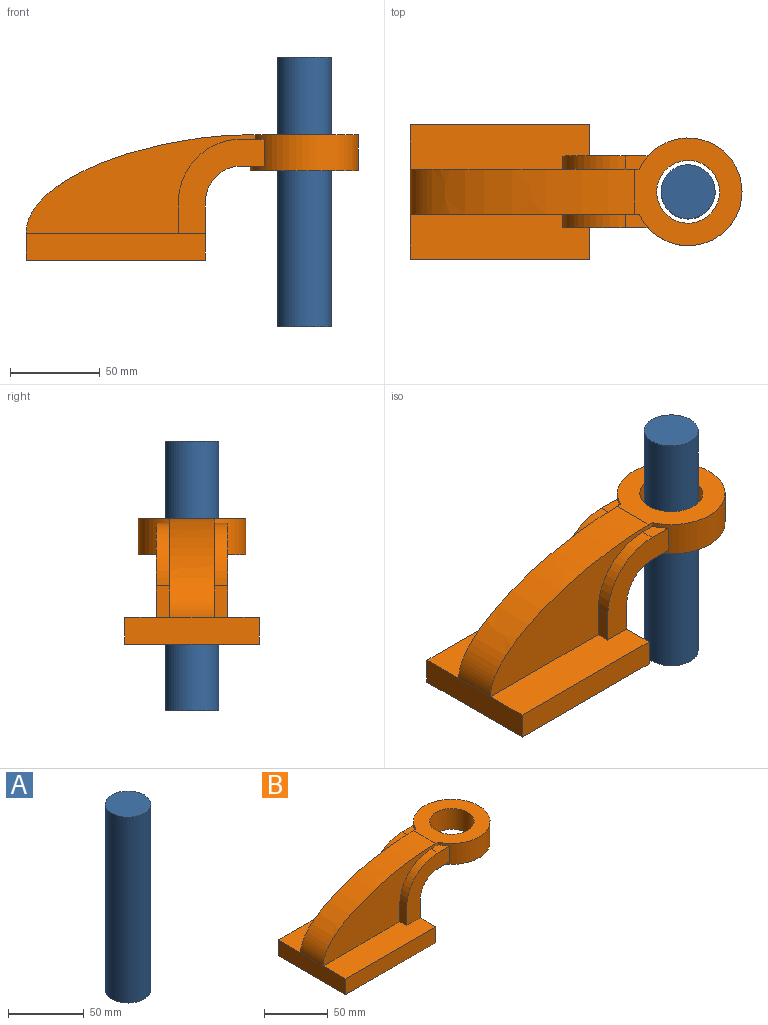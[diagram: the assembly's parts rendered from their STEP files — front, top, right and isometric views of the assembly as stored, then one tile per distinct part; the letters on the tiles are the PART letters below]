
ASSEMBLY  parts=2 mates=1
PART A: 3 faces, bbox 30x30x150 mm
  f0: cylinder r=15mm len=150mm, axis (0,0,-1), area 14137.2mm2, adj f1,f2
  f1: plane 30x30mm, normal (0,0,1), area 706.9mm2, adj f0
  f2: plane 30x30mm, normal (0,0,-1), area 706.9mm2, adj f0
PART B: 24 faces, bbox 185x75x70 mm
  f0: plane 100x25mm, normal (0,0,1), area 2387.5mm2, adj f3,f5,f7,f9,f16,f20
  f1: plane 12.64x7.5mm, normal (0,0,1), area 74.4mm2, adj f2,f16,f20,f22
  f2: cylinder r=35mm len=35mm, axis (0,1,0), area 412.3mm2, adj f1,f3,f16,f20
  f3: plane 17.5x7.5mm, normal (-1,0,0), area 131.2mm2, adj f0,f2,f16,f20
  f4: plane 100x25mm, normal (0,0,1), area 2387.5mm2, adj f5,f7,f8,f14,f15,f19
  f5: plane 75x15mm, normal (-1,0,0), area 1125mm2, adj f0,f4,f6,f8,f9,f17
  f6: plane 100x75mm, normal (0,0,-1), area 7500mm2, adj f5,f7,f8,f9
  f7: plane 75x32.5mm, normal (1,0,0), area 1825mm2, adj f0,f4,f6,f8,f9,f10,f15,f16
  f8: plane 100x15mm, normal (0,-1,0), area 1500mm2, adj f4,f5,f6,f7
  f9: plane 100x15mm, normal (0,1,0), area 1500mm2, adj f0,f5,f6,f7
  f10: cylinder r=20mm len=40mm, axis (0,1,0), area 1256.6mm2, adj f7,f11,f15,f16
  f11: plane 40x12.64mm, normal (0,0,-1), area 296mm2, adj f10,f15,f16,f22
  f12: plane 12.64x7.5mm, normal (0,0,1), area 74.4mm2, adj f13,f15,f19,f22
  f13: cylinder r=35mm len=35mm, axis (0,1,0), area 412.3mm2, adj f12,f14,f15,f19
  f14: plane 17.5x7.5mm, normal (-1,0,0), area 131.2mm2, adj f4,f13,f15,f19
  f15: plane 52.5x47.64mm, normal (0,-1,0), area 1100mm2, adj f4,f7,f10,f11,f12,f13,f14,f22
  f16: plane 52.5x47.64mm, normal (0,1,0), area 1100mm2, adj f0,f1,f2,f3,f7,f10,f11,f22
  f17: extruded ~125x55mm, area 3636.8mm2, adj f5,f18,f19,f20
  f18: plane 60x60mm, normal (0,0,1), area 1887.6mm2, adj f17,f19,f20,f22,f23
  f19: plane 127.73x55mm, normal (0,-1,0), area 3421.1mm2, adj f4,f12,f13,f14,f17,f18,f22
  f20: plane 127.73x55mm, normal (0,1,0), area 3421.1mm2, adj f0,f1,f2,f3,f17,f18,f22
  f21: plane 60x60mm, normal (0,0,-1), area 1865.3mm2, adj f22,f23
  f22: cylinder r=30mm len=60mm, axis (0,0,1), area 3048.7mm2, adj f1,f11,f12,f15,f16,f18,f19,f20
  f23: cylinder r=17.5mm len=35mm, axis (0,0,1), area 2199.1mm2, adj f18,f21
PLACE A rot(axis=(0,0,1),9.7deg) t=(-51.66,47.32,-79.47)mm
PLACE B t=(-53.87,73.38,-47.51)mm fixed
MATE cylindrical A.f0 <-> B.f23  axis (0,0,-1) through (101.13,73.38,-9.47)mm
